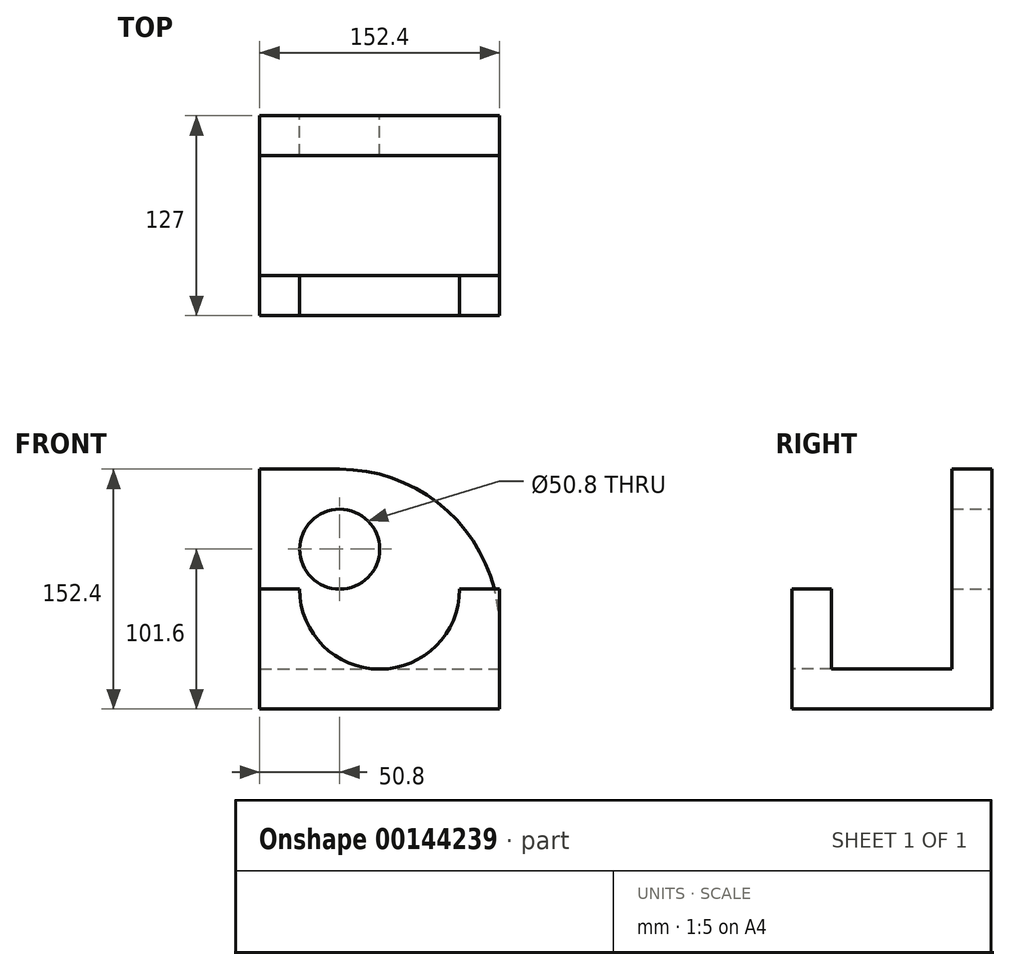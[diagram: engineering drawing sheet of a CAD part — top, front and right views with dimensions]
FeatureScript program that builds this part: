
annotation { "Feature Type Name" : "Feature", "Feature Type Description" : "" }
export const myFeature = defineFeature(function(context is Context, id is Id, definition is map)
    precondition{}
    {
        {
            var Q0;
            Q0=qCreatedBy(makeId("Front.planeOp"),FACE);
            var sketch = newSketch(context, id + "F0", { "sketchPlane" : qUnion([Q0])});
            skLineSegment(sketch, "E0.bottom", {"start": v(76.2, -76.2) * mm, "end": v(-76.2, -76.2) * mm});
            skLineSegment(sketch, "E0.top", {"start": v(76.2, 76.2) * mm, "end": v(-76.2, 76.2) * mm});
            skLineSegment(sketch, "E0.left", {"start": v(76.2, -76.2) * mm, "end": v(76.2, 76.2) * mm});
            skLineSegment(sketch, "E0.right", {"start": v(-76.2, -76.2) * mm, "end": v(-76.2, 76.2) * mm});
            skPoint(sketch, "E0.middle", {"position": v(0, 0) * mm});
            skSolve(sketch);
        }
        {
            var Q0;
            Q0=makeQuery(id+"F0.imprint","IMPRINT",FACE,{"disambiguationData":[TD([[makeQuery(id+"F0.imprint","IMPRINT",EDGE,{"derivedFrom":sQuery(id+"F0.wireOp",EDGE,"E0.bottom")}),-1.0]])]});
            extrude(context, id + "F1", {"entities" : qUnion([Q0]), "endBound" : BoundingType.SYMMETRIC, "depth" : 127 * mm});
        }
        {
            var Q0;
            Q0=makeQuery(id+"F1.opExtrude","SWEPT_FACE",FACE,{"disambiguationData":[OSD([sQuery(id+"F0.wireOp",EDGE,"E0.left")])]});
            var sketch = newSketch(context, id + "F2", { "sketchPlane" : qUnion([Q0])});
            skLineSegment(sketch, "E1.0", {"start": v(-63.5, 76.2) * mm, "end": v(63.5, 76.2) * mm});
            skLineSegment(sketch, "E1.1", {"start": v(-63.5, -76.2) * mm, "end": v(-63.5, 76.2) * mm});
            skLineSegment(sketch, "E1.2", {"start": v(-63.5, -76.2) * mm, "end": v(63.5, -76.2) * mm});
            skLineSegment(sketch, "E1.3", {"start": v(63.5, -76.2) * mm, "end": v(63.5, 76.2) * mm});
            skLineSegment(sketch, "E2", {"start": v(-38.1, 76.2) * mm, "end": v(-38.1, -50.8) * mm});
            skLineSegment(sketch, "E3", {"start": v(-38.1, -50.8) * mm, "end": v(0, -50.8) * mm});
            skLineSegment(sketch, "E4.MirrorCS", {"start": v(38.1, 76.2) * mm, "end": v(38.1, -50.8) * mm});
            skLineSegment(sketch, "E5.MirrorCS", {"start": v(38.1, -50.8) * mm, "end": v(0, -50.8) * mm});
            skSolve(sketch);
        }
        {
            var Q0;
            {var subQ1=sQuery(id+"F2.wireOp",EDGE,"E2");Q0=makeQuery(id+"F2.imprint","IMPRINT",FACE,{"disambiguationData":[TD([[makeQuery(id+"F2.imprint","IMPRINT",EDGE,{"derivedFrom":subQ1}),1.0]])]});}
            extrude(context, id + "F3", {"entities" : qUnion([Q0]), "operationType" : NewBodyOperationType.REMOVE, "endBound" : BoundingType.THROUGH_ALL, "oppositeDirection" : true, "depth" : 25.4 * mm});
        }
        {
            var Q0;
            Q0=makeQuery(id+"F1.opExtrude","CAP_FACE",FACE,{"disambiguationData":[OSD([sQuery(id+"F0.wireOp",EDGE,"E0.bottom"),sQuery(id+"F0.wireOp",EDGE,"E0.top"),sQuery(id+"F0.wireOp",EDGE,"E0.left"),sQuery(id+"F0.wireOp",EDGE,"E0.right")])],"isStart":false});
            var sketch = newSketch(context, id + "F4", { "sketchPlane" : qUnion([Q0])});
            skLineSegment(sketch, "E6.0", {"start": v(76.2, 76.2) * mm, "end": v(-76.2, 76.2) * mm});
            skLineSegment(sketch, "E6.1", {"start": v(-76.2, -76.2) * mm, "end": v(-76.2, 76.2) * mm});
            skLineSegment(sketch, "E6.2", {"start": v(76.2, -76.2) * mm, "end": v(-76.2, -76.2) * mm});
            skLineSegment(sketch, "E6.3", {"start": v(76.2, -76.2) * mm, "end": v(76.2, 76.2) * mm});
            skLineSegment(sketch, "E7", {"start": v(-76.2, 0) * mm, "end": v(76.2, 0) * mm});
            skCircle(sketch, "E8", {"center": v(0, 0) * mm, "radius": 50.8 * mm});
            skSolve(sketch);
        }
        {
            var Q0;
            {var subQ1=sQuery(id+"F4.wireOp",EDGE,"E6.0");Q0=makeQuery(id+"F4.imprint","IMPRINT",FACE,{"disambiguationData":[TD([[makeQuery(id+"F4.imprint","IMPRINT",EDGE,{"derivedFrom":subQ1}),1.0]])]});}
            var Q1;
            {var subQ0=sQuery(id+"F4.wireOp",EDGE,"E8");var subQ1=sQuery(id+"F4.wireOp",EDGE,"E7");var subQ2=makeQuery(id+"F4.imprint","INTERSECT",VERTEX,{"disambiguationData":[OD(0.0)],"derivedFrom":[subQ1,subQ0]});Q1=makeQuery(id+"F4.imprint","IMPRINT",FACE,{"disambiguationData":[TD([[makeQuery(id+"F4.imprint","IMPRINT",EDGE,{"disambiguationData":[TD([[subQ2,-1.0]])],"derivedFrom":subQ1}),1.0]])]});}
            var Q2;
            {var subQ0=sQuery(id+"F4.wireOp",EDGE,"E8");var subQ1=sQuery(id+"F4.wireOp",EDGE,"E7");var subQ2=makeQuery(id+"F4.imprint","INTERSECT",VERTEX,{"disambiguationData":[OD(0.0)],"derivedFrom":[subQ1,subQ0]});Q2=makeQuery(id+"F4.imprint","IMPRINT",FACE,{"disambiguationData":[TD([[makeQuery(id+"F4.imprint","IMPRINT",EDGE,{"disambiguationData":[TD([[subQ2,-1.0]])],"derivedFrom":subQ1}),-1.0]])]});}
            var Q3;
            Q3=makeQuery(id+"F3.boolean.opBoolean","COPY",FACE,{"derivedFrom":makeQuery(id+"F3.opExtrude","SWEPT_FACE",FACE,{"disambiguationData":[OSD([sQuery(id+"F2.wireOp",EDGE,"E2")])]})});
            extrude(context, id + "F5", {"entities" : qUnion([Q0, Q1, Q2]), "operationType" : NewBodyOperationType.REMOVE, "endBound" : BoundingType.UP_TO_SURFACE, "oppositeDirection" : true, "endBoundEntityFace" : qUnion([Q3]), "depth" : 12.4 * mm});
        }
        {
            var Q0;
            Q0=makeQuery(id+"F1.opExtrude","CAP_FACE",FACE,{"disambiguationData":[OSD([sQuery(id+"F0.wireOp",EDGE,"E0.bottom"),sQuery(id+"F0.wireOp",EDGE,"E0.top"),sQuery(id+"F0.wireOp",EDGE,"E0.left"),sQuery(id+"F0.wireOp",EDGE,"E0.right")])],"isStart":true});
            var sketch = newSketch(context, id + "F6", { "sketchPlane" : qUnion([Q0])});
            skLineSegment(sketch, "E9.0", {"start": v(-76.2, 76.2) * mm, "end": v(76.2, 76.2) * mm});
            skLineSegment(sketch, "E9.1", {"start": v(-76.2, -76.2) * mm, "end": v(-76.2, 76.2) * mm});
            skLineSegment(sketch, "E9.2", {"start": v(-76.2, -76.2) * mm, "end": v(76.2, -76.2) * mm});
            skLineSegment(sketch, "E9.3", {"start": v(76.2, -76.2) * mm, "end": v(76.2, 76.2) * mm});
            skPoint(sketch, "E10", {"position": v(25.4, 25.4) * mm});
            skCircle(sketch, "E11", {"center": v(25.4, 25.4) * mm, "radius": 25.4 * mm});
            skCircle(sketch, "E12", {"center": v(25.4, -25.4) * mm, "radius": 101.6 * mm});
            skLineSegment(sketch, "E13", {"start": v(25.4, 25.4) * mm, "end": v(25.4, -25.4) * mm, "construction": true});
            skLineSegment(sketch, "E14", {"start": v(0, 0) * mm, "end": v(0, -23.55) * mm, "construction": true});
            skSolve(sketch);
        }
        {
            var Q0;
            {var subQ0=sQuery(id+"F6.wireOp",EDGE,"E9.1");var subQ1=sQuery(id+"F6.wireOp",EDGE,"E9.0");var subQ2=makeQuery(id+"F6.imprint","INTERSECT",VERTEX,{"derivedFrom":[subQ1,subQ0]});Q0=makeQuery(id+"F6.imprint","IMPRINT",FACE,{"disambiguationData":[TD([[makeQuery(id+"F6.imprint","IMPRINT",EDGE,{"disambiguationData":[TD([[subQ2,-1.0]])],"derivedFrom":subQ1}),-1.0]])]});}
            var Q1;
            Q1=makeQuery(id+"F6.imprint","IMPRINT",FACE,{"disambiguationData":[TD([[makeQuery(id+"F6.imprint","IMPRINT",EDGE,{"derivedFrom":sQuery(id+"F6.wireOp",EDGE,"E11")}),1.0]])]});
            var Q2;
            Q2=makeQuery(id+"F3.boolean.opBoolean","COPY",FACE,{"derivedFrom":makeQuery(id+"F3.opExtrude","SWEPT_FACE",FACE,{"disambiguationData":[OSD([sQuery(id+"F2.wireOp",EDGE,"E4.MirrorCS")])]})});
            extrude(context, id + "F7", {"entities" : qUnion([Q0, Q1]), "operationType" : NewBodyOperationType.REMOVE, "endBound" : BoundingType.UP_TO_SURFACE, "oppositeDirection" : true, "endBoundEntityFace" : qUnion([Q2]), "depth" : 25.4 * mm});
        }
    });
